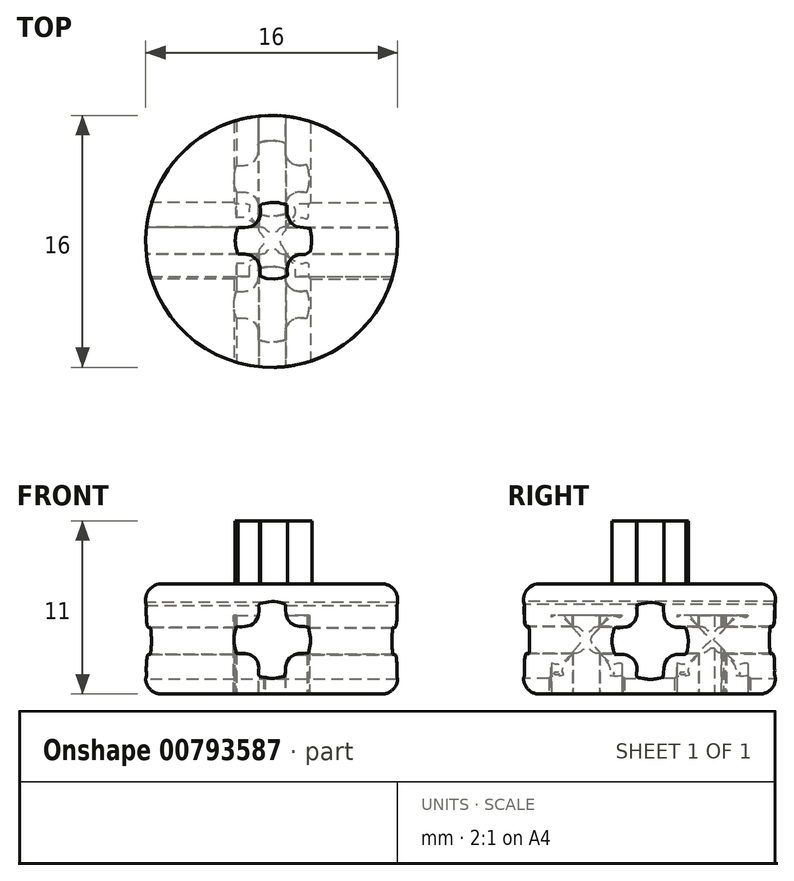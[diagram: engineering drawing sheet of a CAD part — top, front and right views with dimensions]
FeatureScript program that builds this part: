
annotation { "Feature Type Name" : "Feature", "Feature Type Description" : "" }
export const myFeature = defineFeature(function(context is Context, id is Id, definition is map)
    precondition{}
    {
        {
            var Q0;
            Q0=qCreatedBy(makeId("Top.planeOp"),FACE);
            var sketch = newSketch(context, id + "F0", { "sketchPlane" : qUnion([Q0])});
            skCircle(sketch, "E0", {"center": v(0, 0) * mm, "radius": 8 * mm});
            skSolve(sketch);
        }
        {
            var Q0;
            Q0=makeQuery(id+"F0.imprint","IMPRINT",FACE,{"disambiguationData":[TD([[makeQuery(id+"F0.imprint","IMPRINT",EDGE,{"derivedFrom":sQuery(id+"F0.wireOp",EDGE,"E0")}),1.0]])]});
            extrude(context, id + "F1", {"entities" : qUnion([Q0]), "depth" : 7 * mm, "offsetDistance" : 25 * mm});
        }
        {
            var Q0;
            Q0=makeQuery(id+"F1.opExtrude","CAP_FACE",FACE,{"disambiguationData":[OSD([sQuery(id+"F0.wireOp",EDGE,"E0")])],"isStart":false});
            var sketch = newSketch(context, id + "F2", { "sketchPlane" : qUnion([Q0])});
            skFitSpline(sketch, "E1", {"points": [v(-2.15, -0.81) * mm, v(-2.31, 0.07) * mm, v(-2.15, 0.89) * mm], "startDerivative": vector(-0.5, 1.75) * mm, "endDerivative": vector(0.5, 1.65) * mm});
            skFitSpline(sketch, "E2", {"points": [v(-2.15, 0.89) * mm, v(-1.58, 0.89) * mm, v(-1.15, 1.04) * mm, v(-0.85, 1.35) * mm, v(-0.73, 1.7) * mm, v(-0.72, 2.1) * mm, v(-0.72, 2.3) * mm, v(-0.48, 2.39) * mm, v(-0.1, 2.46) * mm, v(0.24, 2.47) * mm, v(0.56, 2.43) * mm, v(0.98, 2.3) * mm], "startDerivative": vector(5.18, -0.26) * mm, "endDerivative": vector(4.37, -1.41) * mm});
            skFitSpline(sketch, "E3", {"points": [v(-2.15, -0.81) * mm, v(-1.85, -0.81) * mm, v(-1.6, -0.81) * mm, v(-1.41, -0.84) * mm, v(-1.07, -1.01) * mm, v(-0.89, -1.21) * mm, v(-0.76, -1.47) * mm, v(-0.72, -1.8) * mm, v(-0.72, -2.23) * mm, v(-0.44, -2.32) * mm, v(-0.16, -2.38) * mm, v(0.17, -2.4) * mm, v(0.46, -2.37) * mm, v(0.72, -2.31) * mm, v(0.98, -2.23) * mm, v(0.98, -2.04) * mm, v(0.98, -1.72) * mm, v(1.01, -1.48) * mm, v(1.1, -1.29) * mm, v(1.27, -1.06) * mm, v(1.4, -0.96) * mm, v(1.58, -0.87) * mm, v(1.83, -0.81) * mm, v(2.08, -0.81) * mm, v(2.4, -0.81) * mm, v(2.48, -0.56) * mm, v(2.54, -0.2) * mm, v(2.55, 0.07) * mm, v(2.53, 0.34) * mm, v(2.46, 0.7) * mm, v(2.4, 0.89) * mm, v(2.08, 0.89) * mm, v(1.8, 0.9) * mm, v(1.47, 1) * mm, v(1.28, 1.13) * mm, v(1.07, 1.4) * mm, v(0.98, 1.81) * mm, v(0.98, 2.3) * mm], "startDerivative": vector(10.87, -0.02) * mm, "endDerivative": vector(0.52, 14.17) * mm});
            skSolve(sketch);
        }
        {
            var Q0;
            Q0=makeQuery(id+"F2.imprint","IMPRINT",FACE,{"disambiguationData":[TD([[makeQuery(id+"F2.imprint","IMPRINT",EDGE,{"derivedFrom":sQuery(id+"F2.wireOp",EDGE,"E1")}),-1.0]])]});
            extrude(context, id + "F3", {"entities" : qUnion([Q0]), "operationType" : NewBodyOperationType.ADD, "depth" : 4 * mm, "offsetDistance" : 25 * mm});
        }
        {
            var Q0;
            Q0=qCreatedBy(makeId("Right.planeOp"),FACE);
            var sketch = newSketch(context, id + "F4", { "sketchPlane" : qUnion([Q0])});
            skFitSpline(sketch, "E4", {"points": [v(-2.22, 2.52) * mm, v(-2.39, 3.4) * mm, v(-2.22, 4.22) * mm], "startDerivative": vector(-0.5, 1.75) * mm, "endDerivative": vector(0.5, 1.65) * mm});
            skFitSpline(sketch, "E5", {"points": [v(-2.22, 4.22) * mm, v(-1.66, 4.22) * mm, v(-1.22, 4.37) * mm, v(-0.92, 4.68) * mm, v(-0.8, 5.03) * mm, v(-0.8, 5.44) * mm, v(-0.8, 5.64) * mm, v(-0.56, 5.72) * mm, v(-0.17, 5.8) * mm, v(0.17, 5.8) * mm, v(0.49, 5.76) * mm, v(0.9, 5.64) * mm], "startDerivative": vector(5.18, -0.26) * mm, "endDerivative": vector(4.37, -1.41) * mm});
            skFitSpline(sketch, "E6", {"points": [v(-2.22, 2.52) * mm, v(-1.93, 2.52) * mm, v(-1.68, 2.52) * mm, v(-1.49, 2.5) * mm, v(-1.15, 2.32) * mm, v(-0.96, 2.12) * mm, v(-0.84, 1.86) * mm, v(-0.8, 1.54) * mm, v(-0.8, 1.1) * mm, v(-0.52, 1.01) * mm, v(-0.23, 0.95) * mm, v(0.1, 0.93) * mm, v(0.38, 0.96) * mm, v(0.65, 1.02) * mm, v(0.9, 1.1) * mm, v(0.9, 1.3) * mm, v(0.9, 1.6) * mm, v(0.94, 1.86) * mm, v(1.02, 2.05) * mm, v(1.2, 2.27) * mm, v(1.33, 2.38) * mm, v(1.5, 2.47) * mm, v(1.76, 2.52) * mm, v(2, 2.52) * mm, v(2.32, 2.52) * mm, v(2.4, 2.78) * mm, v(2.46, 3.13) * mm, v(2.47, 3.4) * mm, v(2.46, 3.67) * mm, v(2.38, 4.04) * mm, v(2.32, 4.22) * mm, v(2, 4.22) * mm, v(1.73, 4.23) * mm, v(1.4, 4.33) * mm, v(1.2, 4.46) * mm, v(1, 4.73) * mm, v(0.9, 5.15) * mm, v(0.9, 5.64) * mm], "startDerivative": vector(10.87, -0.02) * mm, "endDerivative": vector(0.52, 14.17) * mm});
            skSolve(sketch);
        }
        {
            var Q0;
            Q0=qSketchRegion(id+"F4",true);
            extrude(context, id + "F5", {"entities" : qUnion([Q0]), "operationType" : NewBodyOperationType.REMOVE, "oppositeDirection" : true, "depth" : 25 * mm, "offsetDistance" : 25 * mm, "hasSecondDirection" : true, "secondDirectionOppositeDirection" : false, "secondDirectionDepth" : 25 * mm});
        }
        {
            var Q0;
            Q0=qCreatedBy(makeId("Front.planeOp"),FACE);
            var sketch = newSketch(context, id + "F6", { "sketchPlane" : qUnion([Q0])});
            skFitSpline(sketch, "E7", {"points": [v(-2.23, 2.59) * mm, v(-2.4, 3.47) * mm, v(-2.23, 4.29) * mm], "startDerivative": vector(-0.5, 1.75) * mm, "endDerivative": vector(0.5, 1.65) * mm});
            skFitSpline(sketch, "E8", {"points": [v(-2.23, 4.29) * mm, v(-1.67, 4.29) * mm, v(-1.23, 4.43) * mm, v(-0.93, 4.75) * mm, v(-0.82, 5.1) * mm, v(-0.81, 5.5) * mm, v(-0.81, 5.7) * mm, v(-0.57, 5.79) * mm, v(-0.18, 5.86) * mm, v(0.16, 5.87) * mm, v(0.48, 5.83) * mm, v(0.9, 5.7) * mm], "startDerivative": vector(5.18, -0.26) * mm, "endDerivative": vector(4.37, -1.41) * mm});
            skFitSpline(sketch, "E9", {"points": [v(-2.23, 2.59) * mm, v(-1.94, 2.59) * mm, v(-1.69, 2.58) * mm, v(-1.5, 2.55) * mm, v(-1.16, 2.38) * mm, v(-0.97, 2.19) * mm, v(-0.85, 1.92) * mm, v(-0.81, 1.6) * mm, v(-0.81, 1.16) * mm, v(-0.53, 1.08) * mm, v(-0.24, 1.02) * mm, v(0.09, 1) * mm, v(0.37, 1.02) * mm, v(0.64, 1.08) * mm, v(0.9, 1.16) * mm, v(0.9, 1.36) * mm, v(0.9, 1.67) * mm, v(0.93, 1.92) * mm, v(1, 2.11) * mm, v(1.18, 2.33) * mm, v(1.32, 2.44) * mm, v(1.5, 2.53) * mm, v(1.75, 2.58) * mm, v(2, 2.59) * mm, v(2.31, 2.59) * mm, v(2.4, 2.84) * mm, v(2.45, 3.2) * mm, v(2.46, 3.47) * mm, v(2.45, 3.73) * mm, v(2.37, 4.1) * mm, v(2.31, 4.29) * mm, v(2, 4.29) * mm, v(1.72, 4.3) * mm, v(1.39, 4.4) * mm, v(1.2, 4.53) * mm, v(0.99, 4.8) * mm, v(0.9, 5.2) * mm, v(0.9, 5.7) * mm], "startDerivative": vector(10.87, -0.02) * mm, "endDerivative": vector(0.52, 14.17) * mm});
            skSolve(sketch);
        }
        {
            var Q0;
            Q0=qSketchRegion(id+"F6",true);
            extrude(context, id + "F7", {"entities" : qUnion([Q0]), "operationType" : NewBodyOperationType.REMOVE, "oppositeDirection" : true, "depth" : 25 * mm, "offsetDistance" : 25 * mm, "hasSecondDirection" : true, "secondDirectionOppositeDirection" : false, "secondDirectionDepth" : 25 * mm});
        }
        {
            var Q0;
            Q0=makeQuery(id+"F1.opExtrude","CAP_FACE",FACE,{"disambiguationData":[OSD([sQuery(id+"F0.wireOp",EDGE,"E0")])],"isStart":true});
            var sketch = newSketch(context, id + "F8", { "sketchPlane" : qUnion([Q0])});
            skFitSpline(sketch, "E10", {"points": [v(-2.26, 3.17) * mm, v(-2.43, 4.05) * mm, v(-2.26, 4.86) * mm], "startDerivative": vector(-0.5, 1.75) * mm, "endDerivative": vector(0.5, 1.64) * mm});
            skFitSpline(sketch, "E11", {"points": [v(-2.26, 4.86) * mm, v(-1.7, 4.87) * mm, v(-1.26, 5.01) * mm, v(-0.96, 5.32) * mm, v(-0.85, 5.67) * mm, v(-0.84, 6.08) * mm, v(-0.84, 6.28) * mm, v(-0.6, 6.36) * mm, v(-0.22, 6.43) * mm, v(0.12, 6.44) * mm, v(0.44, 6.4) * mm, v(0.85, 6.28) * mm], "startDerivative": vector(5.17, -0.26) * mm, "endDerivative": vector(4.36, -1.4) * mm});
            skFitSpline(sketch, "E12", {"points": [v(-2.26, 3.17) * mm, v(-1.96, 3.17) * mm, v(-1.72, 3.17) * mm, v(-1.53, 3.14) * mm, v(-1.19, 2.97) * mm, v(-1, 2.77) * mm, v(-0.88, 2.51) * mm, v(-0.84, 2.2) * mm, v(-0.84, 1.75) * mm, v(-0.56, 1.66) * mm, v(-0.28, 1.6) * mm, v(0.05, 1.59) * mm, v(0.34, 1.61) * mm, v(0.6, 1.67) * mm, v(0.85, 1.75) * mm, v(0.85, 1.95) * mm, v(0.85, 2.26) * mm, v(0.89, 2.5) * mm, v(0.97, 2.7) * mm, v(1.14, 2.92) * mm, v(1.28, 3.03) * mm, v(1.46, 3.11) * mm, v(1.7, 3.17) * mm, v(1.95, 3.17) * mm, v(2.27, 3.17) * mm, v(2.35, 3.42) * mm, v(2.4, 3.77) * mm, v(2.42, 4.05) * mm, v(2.4, 4.31) * mm, v(2.33, 4.68) * mm, v(2.27, 4.86) * mm, v(1.95, 4.86) * mm, v(1.67, 4.87) * mm, v(1.35, 4.97) * mm, v(1.15, 5.1) * mm, v(0.95, 5.37) * mm, v(0.85, 5.78) * mm, v(0.85, 6.28) * mm], "startDerivative": vector(10.83, -0.02) * mm, "endDerivative": vector(0.52, 14.12) * mm});
            skFitSpline(sketch, "E13", {"points": [v(-2.26, -4.83) * mm, v(-2.43, -3.95) * mm, v(-2.26, -3.14) * mm], "startDerivative": vector(-0.5, 1.75) * mm, "endDerivative": vector(0.5, 1.64) * mm});
            skFitSpline(sketch, "E14", {"points": [v(-2.26, -3.14) * mm, v(-1.7, -3.13) * mm, v(-1.26, -2.99) * mm, v(-0.96, -2.68) * mm, v(-0.85, -2.33) * mm, v(-0.84, -1.92) * mm, v(-0.84, -1.72) * mm, v(-0.6, -1.64) * mm, v(-0.22, -1.57) * mm, v(0.12, -1.56) * mm, v(0.44, -1.6) * mm, v(0.85, -1.72) * mm], "startDerivative": vector(5.17, -0.26) * mm, "endDerivative": vector(4.36, -1.4) * mm});
            skFitSpline(sketch, "E15", {"points": [v(-2.26, -4.83) * mm, v(-1.96, -4.83) * mm, v(-1.72, -4.83) * mm, v(-1.53, -4.86) * mm, v(-1.19, -5.03) * mm, v(-1, -5.23) * mm, v(-0.88, -5.49) * mm, v(-0.84, -5.8) * mm, v(-0.84, -6.25) * mm, v(-0.56, -6.34) * mm, v(-0.28, -6.4) * mm, v(0.05, -6.41) * mm, v(0.34, -6.39) * mm, v(0.6, -6.33) * mm, v(0.85, -6.25) * mm, v(0.85, -6.05) * mm, v(0.85, -5.74) * mm, v(0.89, -5.5) * mm, v(0.97, -5.3) * mm, v(1.14, -5.08) * mm, v(1.28, -4.97) * mm, v(1.46, -4.89) * mm, v(1.7, -4.83) * mm, v(1.95, -4.83) * mm, v(2.27, -4.83) * mm, v(2.35, -4.58) * mm, v(2.33, -4.58) * mm, v(2.42, -3.95) * mm, v(2.4, -3.69) * mm, v(2.33, -3.32) * mm, v(2.27, -3.14) * mm, v(1.95, -3.14) * mm, v(1.67, -3.13) * mm, v(1.35, -3.03) * mm, v(1.15, -2.9) * mm, v(0.95, -2.63) * mm, v(0.85, -2.22) * mm, v(0.85, -1.72) * mm], "startDerivative": vector(10.83, -0.02) * mm, "endDerivative": vector(0.52, 14.12) * mm});
            skCircle(sketch, "E16", {"center": v(0, 4) * mm, "radius": 2.4 * mm});
            skCircle(sketch, "E17", {"center": v(0, -4) * mm, "radius": 2.4 * mm});
            skLineSegment(sketch, "E18", {"start": v(0, 4) * mm, "end": v(0, -4) * mm});
            skPoint(sketch, "E19", {"position": v(0, 0) * mm});
            skSolve(sketch);
        }
        {
            var Q0;
            Q0=makeQuery(id+"F8.imprint","IMPRINT",FACE,{"disambiguationData":[TD([[makeQuery(id+"F8.imprint","IMPRINT",EDGE,{"derivedFrom":sQuery(id+"F8.wireOp",EDGE,"E10")}),-1.0]])]});
            var Q1;
            {var subQ0=sQuery(id+"F8.wireOp",EDGE,"E16");var subQ4=sQuery(id+"F8.wireOp",EDGE,"E10");var subQ5=makeQuery(id+"F8.imprint","INTERSECT",VERTEX,{"disambiguationData":[OD(0.0)],"derivedFrom":[subQ4,subQ0]});Q1=makeQuery(id+"F8.imprint","IMPRINT",FACE,{"disambiguationData":[TD([[makeQuery(id+"F8.imprint","IMPRINT",EDGE,{"disambiguationData":[TD([[subQ5,-1.0]])],"derivedFrom":subQ4}),-1.0]])]});}
            var Q2;
            {var subQ0=sQuery(id+"F8.wireOp",EDGE,"E17");var subQ1=sQuery(id+"F8.wireOp",EDGE,"E13");var subQ17=makeQuery(id+"F8.imprint","INTERSECT",VERTEX,{"disambiguationData":[OD(0.0)],"derivedFrom":[subQ1,subQ0]});Q2=makeQuery(id+"F8.imprint","IMPRINT",FACE,{"disambiguationData":[TD([[makeQuery(id+"F8.imprint","IMPRINT",EDGE,{"disambiguationData":[TD([[subQ17,-1.0]])],"derivedFrom":subQ1}),-1.0]])]});}
            extrude(context, id + "F9", {"entities" : qUnion([Q0, Q1, Q2]), "operationType" : NewBodyOperationType.REMOVE, "oppositeDirection" : true, "depth" : 5 * mm, "offsetDistance" : 25 * mm});
        }
        {
            var Q0;
            Q0=makeQuery(id+"F1.opExtrude","CAP_EDGE",EDGE,{"disambiguationData":[OSD([sQuery(id+"F0.wireOp",EDGE,"E0")])],"isStart":true});
            var Q1;
            Q1=makeQuery(id+"F1.opExtrude","CAP_EDGE",EDGE,{"disambiguationData":[OSD([sQuery(id+"F0.wireOp",EDGE,"E0")])],"isStart":false});
            fillet(context, id + "F10", {"entities" : qUnion([Q0, Q1]), "radius" : 1 * mm, "tangentPropagation" : true, "allowEdgeOverflow" : false});
        }
    });
